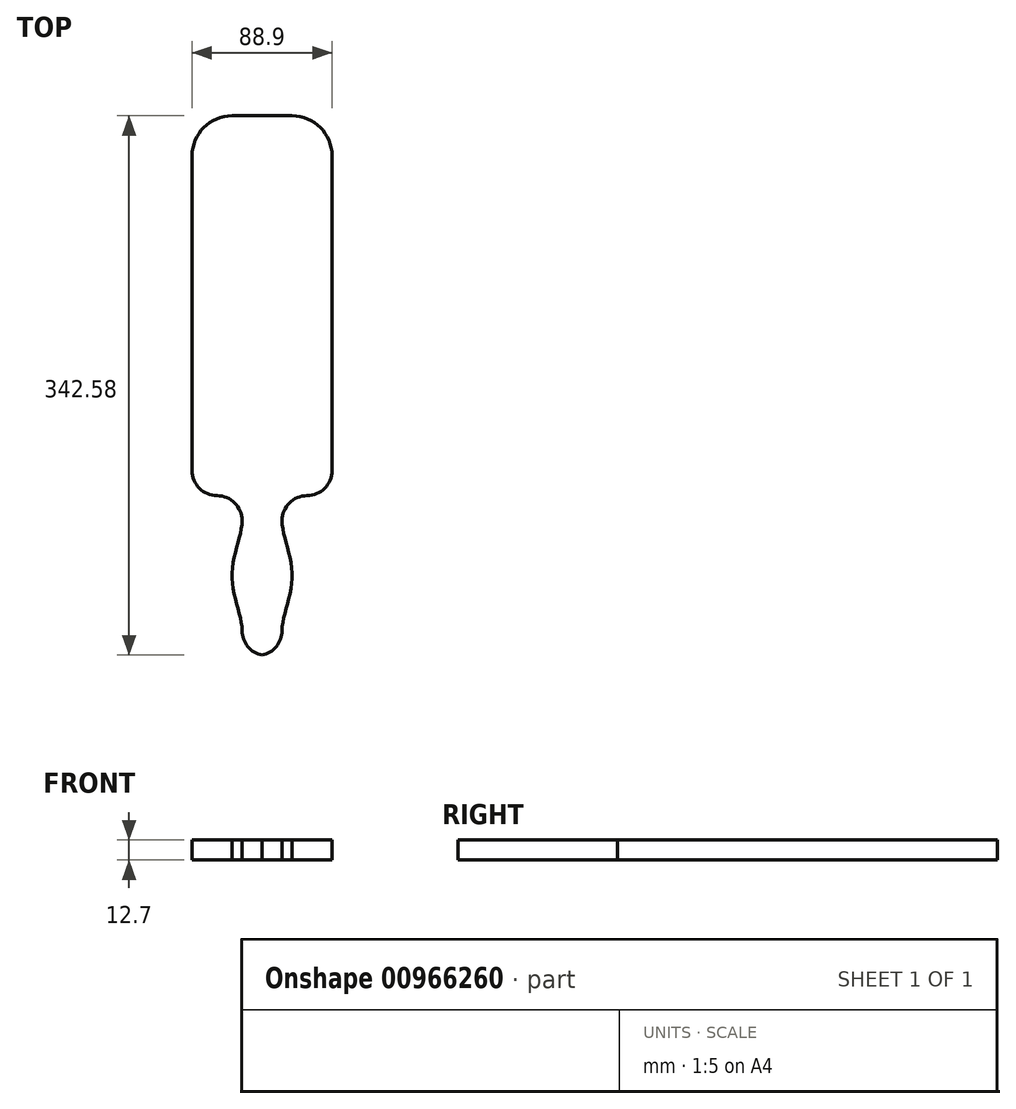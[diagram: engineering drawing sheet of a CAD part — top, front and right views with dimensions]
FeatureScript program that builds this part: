
annotation { "Feature Type Name" : "Feature", "Feature Type Description" : "" }
export const myFeature = defineFeature(function(context is Context, id is Id, definition is map)
    precondition{}
    {
        {
            var Q0;
            Q0=qCreatedBy(makeId("Top.planeOp"),FACE);
            var sketch = newSketch(context, id + "F0", { "sketchPlane" : qUnion([Q0])});
            skLineSegment(sketch, "E0.bottom", {"start": v(25.4, 342.9) * mm, "end": v(63.5, 342.9) * mm});
            skLineSegment(sketch, "E0.top", {"start": v(41.28, 0) * mm, "end": v(47.62, 0) * mm});
            skLineSegment(sketch, "E0.left", {"start": v(0, 317.5) * mm, "end": v(0, 117.48) * mm});
            skLineSegment(sketch, "E0.right", {"start": v(88.9, 317.5) * mm, "end": v(88.9, 117.48) * mm});
            skLineSegment(sketch, "E1.top", {"start": v(15.88, 101.6) * mm, "end": v(15.88, 101.6) * mm});
            skLineSegment(sketch, "E1.right", {"start": v(31.75, 15.88) * mm, "end": v(31.75, 85.73) * mm});
            skLineSegment(sketch, "E2.top", {"start": v(73.03, 101.6) * mm, "end": v(73.02, 101.6) * mm});
            skLineSegment(sketch, "E2.right", {"start": v(57.15, 15.87) * mm, "end": v(57.15, 85.73) * mm});
            skPoint(sketch, "E2.bottom.start.orphan", {"position": v(88.9, 0) * mm});
            skPoint(sketch, "E3.visualSharp", {"position": v(0, 101.6) * mm});
            skArc(sketch, "E3.filletArc", {"start": v(0, 117.48) * mm, "mid": v(4.65, 106.25) * mm, "end": v(15.88, 101.6) * mm});
            skPoint(sketch, "E4.visualSharp", {"position": v(88.9, 101.6) * mm});
            skArc(sketch, "E4.filletArc", {"start": v(73.03, 101.6) * mm, "mid": v(84.25, 106.25) * mm, "end": v(88.9, 117.48) * mm});
            skPoint(sketch, "E5.visualSharp", {"position": v(57.15, 101.6) * mm});
            skArc(sketch, "E5.filletArc", {"start": v(73.02, 101.6) * mm, "mid": v(61.8, 96.95) * mm, "end": v(57.15, 85.73) * mm});
            skPoint(sketch, "E6.visualSharp", {"position": v(31.75, 101.6) * mm});
            skArc(sketch, "E6.filletArc", {"start": v(31.75, 85.73) * mm, "mid": v(27.1, 96.95) * mm, "end": v(15.88, 101.6) * mm});
            skPoint(sketch, "E7.visualSharp", {"position": v(31.75, 0) * mm});
            skArc(sketch, "E7.filletArc", {"start": v(31.75, 15.87) * mm, "mid": v(36.4, 4.65) * mm, "end": v(47.62, 0) * mm});
            skPoint(sketch, "E8.visualSharp", {"position": v(57.15, 0) * mm});
            skArc(sketch, "E8.filletArc", {"start": v(41.28, 0) * mm, "mid": v(52.5, 4.65) * mm, "end": v(57.15, 15.87) * mm});
            skPoint(sketch, "E9.visualSharp", {"position": v(88.9, 342.9) * mm});
            skArc(sketch, "E9.filletArc", {"start": v(88.9, 317.5) * mm, "mid": v(81.46, 335.46) * mm, "end": v(63.5, 342.9) * mm});
            skPoint(sketch, "E10.visualSharp", {"position": v(0, 342.9) * mm});
            skArc(sketch, "E10.filletArc", {"start": v(25.4, 342.9) * mm, "mid": v(7.44, 335.46) * mm, "end": v(0, 317.5) * mm});
            skFitSpline(sketch, "E11", {"points": [v(31.75, 85.73) * mm, v(25.4, 50.8) * mm, v(31.75, 15.88) * mm], "startDerivative": vector(0, -57.15) * mm, "endDerivative": vector(0, -57.15) * mm});
            skFitSpline(sketch, "E12", {"points": [v(57.15, 85.73) * mm, v(63.5, 50.8) * mm, v(57.15, 15.87) * mm], "startDerivative": vector(0, -57.15) * mm, "endDerivative": vector(0, -57.15) * mm});
            skSolve(sketch);
        }
        {
            var Q0;
            Q0=makeQuery(id+"F0.imprint","IMPRINT",FACE,{"disambiguationData":[TD([[makeQuery(id+"F0.imprint","IMPRINT",EDGE,{"derivedFrom":sQuery(id+"F0.wireOp",EDGE,"E1.right")}),1.0]])]});
            var Q1;
            Q1=makeQuery(id+"F0.imprint","IMPRINT",FACE,{"disambiguationData":[TD([[makeQuery(id+"F0.imprint","IMPRINT",EDGE,{"derivedFrom":sQuery(id+"F0.wireOp",EDGE,"E2.right")}),-1.0]])]});
            var Q2;
            Q2=makeQuery(id+"F0.imprint","IMPRINT",FACE,{"disambiguationData":[TD([[makeQuery(id+"F0.imprint","IMPRINT",EDGE,{"derivedFrom":sQuery(id+"F0.wireOp",EDGE,"E0.bottom")}),-1.0]])]});
            extrude(context, id + "F1", {"entities" : qUnion([Q0, Q1, Q2]), "depth" : 12.7 * mm, "offsetDistance" : 25.4 * mm});
        }
    });
